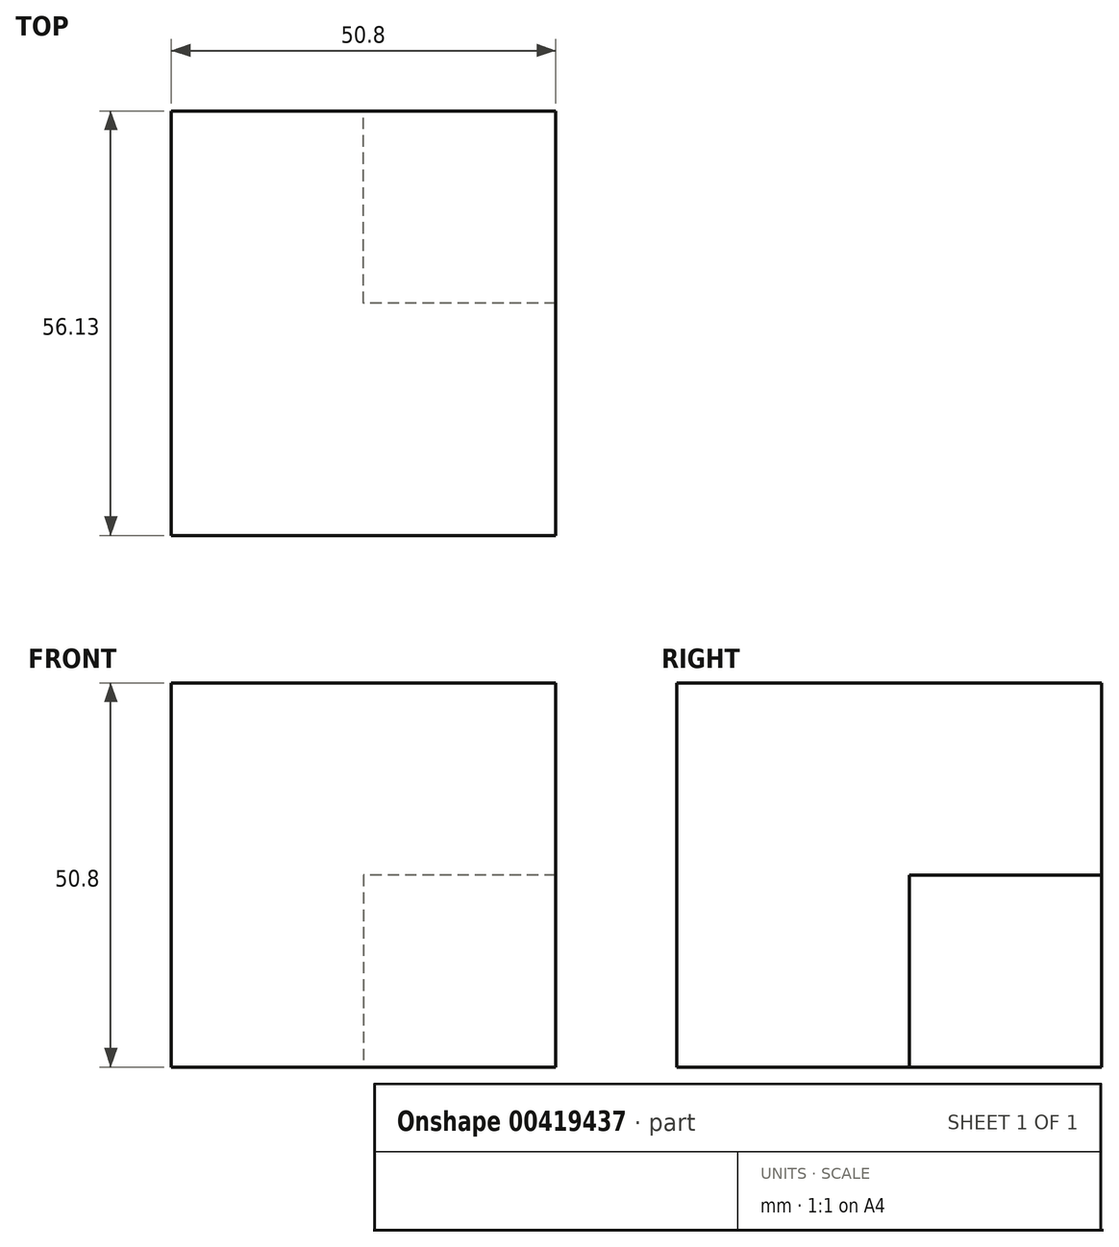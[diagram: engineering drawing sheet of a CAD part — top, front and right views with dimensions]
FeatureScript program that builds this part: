
annotation { "Feature Type Name" : "Feature", "Feature Type Description" : "" }
export const myFeature = defineFeature(function(context is Context, id is Id, definition is map)
    precondition{}
    {
        {
            var Q0;
            Q0=qCreatedBy(makeId("Front.planeOp"),FACE);
            var sketch = newSketch(context, id + "F0", { "sketchPlane" : qUnion([Q0])});
            skLineSegment(sketch, "E0.bottom", {"start": v(25.4, 25.4) * mm, "end": v(-25.4, 25.4) * mm});
            skLineSegment(sketch, "E0.top", {"start": v(25.4, -25.4) * mm, "end": v(-25.4, -25.4) * mm});
            skLineSegment(sketch, "E0.left", {"start": v(25.4, 25.4) * mm, "end": v(25.4, -25.4) * mm});
            skLineSegment(sketch, "E0.right", {"start": v(-25.4, 25.4) * mm, "end": v(-25.4, -25.4) * mm});
            skPoint(sketch, "E0.middle", {"position": v(0, 0) * mm});
            skSolve(sketch);
        }
        {
            var Q0;
            Q0 = qSketchRegion(id + "F0", true);
            extrude(context, id + "F1", {"entities" : qUnion([Q0]), "oppositeDirection" : true, "depth" : 56.13 * mm});
        }
        {
            var Q0;
            Q0=makeQuery(id+"F1.opExtrude","CAP_FACE",FACE,{"disambiguationData":[OSD([sQuery(id+"F0.wireOp",EDGE,"E0.bottom"),sQuery(id+"F0.wireOp",EDGE,"E0.top"),sQuery(id+"F0.wireOp",EDGE,"E0.left"),sQuery(id+"F0.wireOp",EDGE,"E0.right")])],"isStart":false});
            var sketch = newSketch(context, id + "F2", { "sketchPlane" : qUnion([Q0])});
            skLineSegment(sketch, "E1.bottom", {"start": v(-25.4, 0) * mm, "end": v(0, 0) * mm});
            skLineSegment(sketch, "E1.top", {"start": v(-25.4, -25.4) * mm, "end": v(0, -25.4) * mm});
            skLineSegment(sketch, "E1.left", {"start": v(0, 0) * mm, "end": v(0, -25.4) * mm});
            skLineSegment(sketch, "E1.right", {"start": v(-25.4, 0) * mm, "end": v(-25.4, -25.4) * mm});
            skSolve(sketch);
        }
        {
            var Q0;
            Q0 = qSketchRegion(id + "F2", true);
            extrude(context, id + "F3", {"entities" : qUnion([Q0]), "operationType" : NewBodyOperationType.REMOVE, "oppositeDirection" : true, "depth" : 25.4 * mm});
        }
    });
